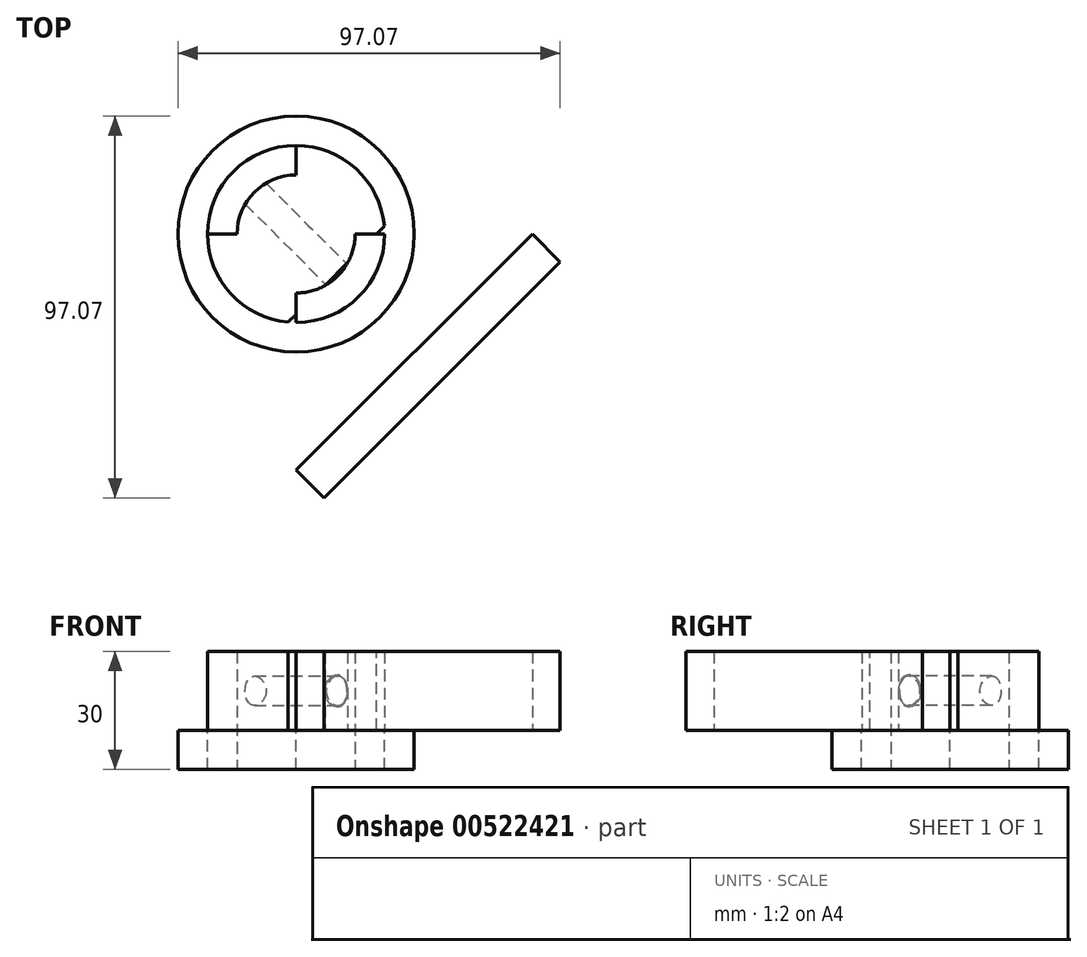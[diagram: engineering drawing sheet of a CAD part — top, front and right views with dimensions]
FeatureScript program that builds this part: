
annotation { "Feature Type Name" : "Feature", "Feature Type Description" : "" }
export const myFeature = defineFeature(function(context is Context, id is Id, definition is map)
    precondition{}
    {
        {
            var Q0;
            Q0=qCreatedBy(makeId("Top.planeOp"),FACE);
            var sketch = newSketch(context, id + "F0", { "sketchPlane" : qUnion([Q0])});
            skCircle(sketch, "E0", {"center": v(0, 0) * mm, "radius": 15 * mm});
            skCircle(sketch, "E1", {"center": v(0, 0) * mm, "radius": 30 * mm});
            skCircle(sketch, "E2", {"center": v(0, 0) * mm, "radius": 22.5 * mm});
            skLineSegment(sketch, "E3", {"start": v(0, 15) * mm, "end": v(0, 22.5) * mm});
            skLineSegment(sketch, "E4", {"start": v(0, 22.5) * mm, "end": v(0, 30) * mm, "construction": true});
            skLineSegment(sketch, "E5", {"start": v(-22.5, 0) * mm, "end": v(-15, 0) * mm});
            skLineSegment(sketch, "E6", {"start": v(0, -15) * mm, "end": v(0, -22.5) * mm});
            skLineSegment(sketch, "E7", {"start": v(15, 0) * mm, "end": v(22.5, 0) * mm});
            skSolve(sketch);
        }
        {
            var Q0;
            {var subQ0=sQuery(id+"F0.wireOp",EDGE,"E0");var subQ1=makeQuery(id+"F0.imprint","INTERSECT",VERTEX,{"derivedFrom":[subQ0,sQuery(id+"F0.wireOp",EDGE,"E3")]});Q0=makeQuery(id+"F0.imprint","IMPRINT",FACE,{"disambiguationData":[TD([[makeQuery(id+"F0.imprint","IMPRINT",EDGE,{"disambiguationData":[TD([[subQ1,1.0]])],"derivedFrom":subQ0}),1.0]])]});}
            var Q1;
            {var subQ0=sQuery(id+"F0.wireOp",EDGE,"E3");Q1=makeQuery(id+"F0.imprint","IMPRINT",FACE,{"disambiguationData":[TD([[makeQuery(id+"F0.imprint","IMPRINT",EDGE,{"derivedFrom":subQ0}),-1.0]])]});}
            var Q2;
            {var subQ0=sQuery(id+"F0.wireOp",EDGE,"E5");Q2=makeQuery(id+"F0.imprint","IMPRINT",FACE,{"disambiguationData":[TD([[makeQuery(id+"F0.imprint","IMPRINT",EDGE,{"derivedFrom":subQ0}),-1.0]])]});}
            extrude(context, id + "F1", {"entities" : qUnion([Q0, Q1, Q2]), "depth" : 20 * mm, "offsetDistance" : 25 * mm});
        }
        {
            var Q0;
            Q0=makeQuery(id+"F0.imprint","IMPRINT",FACE,{"disambiguationData":[TD([[makeQuery(id+"F0.imprint","IMPRINT",EDGE,{"derivedFrom":sQuery(id+"F0.wireOp",EDGE,"E1")}),1.0]])]});
            var Q1;
            {var subQ0=sQuery(id+"F0.wireOp",EDGE,"E3");Q1=makeQuery(id+"F0.imprint","IMPRINT",FACE,{"disambiguationData":[TD([[makeQuery(id+"F0.imprint","IMPRINT",EDGE,{"derivedFrom":subQ0}),-1.0]])]});}
            var Q2;
            {var subQ0=sQuery(id+"F0.wireOp",EDGE,"E0");var subQ1=makeQuery(id+"F0.imprint","INTERSECT",VERTEX,{"derivedFrom":[subQ0,sQuery(id+"F0.wireOp",EDGE,"E3")]});Q2=makeQuery(id+"F0.imprint","IMPRINT",FACE,{"disambiguationData":[TD([[makeQuery(id+"F0.imprint","IMPRINT",EDGE,{"disambiguationData":[TD([[subQ1,1.0]])],"derivedFrom":subQ0}),1.0]])]});}
            var Q3;
            {var subQ0=sQuery(id+"F0.wireOp",EDGE,"E5");Q3=makeQuery(id+"F0.imprint","IMPRINT",FACE,{"disambiguationData":[TD([[makeQuery(id+"F0.imprint","IMPRINT",EDGE,{"derivedFrom":subQ0}),-1.0]])]});}
            extrude(context, id + "F2", {"entities" : qUnion([Q0, Q1, Q2, Q3]), "operationType" : NewBodyOperationType.ADD, "oppositeDirection" : true, "depth" : 10 * mm, "offsetDistance" : 25 * mm});
        }
        {
            var Q0;
            Q0=qCreatedBy(makeId("Top.planeOp"),FACE);
            var sketch = newSketch(context, id + "F3", { "sketchPlane" : qUnion([Q0])});
            skLineSegment(sketch, "E8", {"start": v(0, 0) * mm, "end": v(0, -60) * mm, "construction": true});
            skLineSegment(sketch, "E9", {"start": v(60, 0) * mm, "end": v(0, -60) * mm});
            skLineSegment(sketch, "E10.MirrorCS", {"start": v(7.07, -67.07) * mm, "end": v(67.07, -7.07) * mm});
            skLineSegment(sketch, "E11.MirrorCS", {"start": v(67.07, -7.07) * mm, "end": v(60, 0) * mm});
            skLineSegment(sketch, "E12.MirrorCS", {"start": v(0, -60) * mm, "end": v(7.07, -67.07) * mm});
            skPoint(sketch, "E13.end.orphan", {"position": v(-60, 0) * mm});
            skPoint(sketch, "E13.start.orphan", {"position": v(-67.07, -7.07) * mm});
            skPoint(sketch, "E14.end.orphan", {"position": v(-7.07, -67.07) * mm});
            skPoint(sketch, "E14.start.orphan", {"position": v(0, -60) * mm});
            skLineSegment(sketch, "E15", {"start": v(0, 0) * mm, "end": v(60, 0) * mm, "construction": true});
            skSolve(sketch);
        }
        {
            var Q0;
            Q0=makeQuery(id+"F3.imprint","IMPRINT",FACE,{"disambiguationData":[TD([[makeQuery(id+"F3.imprint","IMPRINT",EDGE,{"derivedFrom":sQuery(id+"F3.wireOp",EDGE,"E9")}),1.0]])]});
            extrude(context, id + "F4", {"entities" : qUnion([Q0]), "depth" : 20 * mm, "offsetDistance" : 25 * mm});
        }
        {
            var Q0;
            Q0=makeQuery(id+"F4.opExtrude","SWEPT_FACE",FACE,{"disambiguationData":[OSD([sQuery(id+"F3.wireOp",EDGE,"E9")])]});
            var sketch = newSketch(context, id + "F5", { "sketchPlane" : qUnion([Q0])});
            skLineSegment(sketch, "E16", {"start": v(-42.43, 20) * mm, "end": v(-42.43, 0) * mm});
            skLineSegment(sketch, "E17", {"start": v(0, 20) * mm, "end": v(0, 0) * mm});
            skLineSegment(sketch, "E18", {"start": v(-42.43, 10) * mm, "end": v(-42.43, 10) * mm});
            skCircle(sketch, "E19", {"center": v(0, 10) * mm, "radius": 3.75 * mm});
            skCircle(sketch, "E20", {"center": v(0, 10) * mm, "radius": 4 * mm});
            skSolve(sketch);
        }
        {
            var Q0;
            {var subQ0=sQuery(id+"F5.wireOp",EDGE,"E19");var subQ1=sQuery(id+"F5.wireOp",EDGE,"E17");var subQ2=makeQuery(id+"F5.imprint","INTERSECT",VERTEX,{"disambiguationData":[OD(0.0)],"derivedFrom":[subQ1,subQ0]});Q0=makeQuery(id+"F5.imprint","IMPRINT",FACE,{"disambiguationData":[TD([[makeQuery(id+"F5.imprint","IMPRINT",EDGE,{"disambiguationData":[TD([[subQ2,-1.0]])],"derivedFrom":subQ1}),-1.0]])]});}
            var Q1;
            {var subQ0=sQuery(id+"F5.wireOp",EDGE,"E19");var subQ1=sQuery(id+"F5.wireOp",EDGE,"E17");var subQ2=makeQuery(id+"F5.imprint","INTERSECT",VERTEX,{"disambiguationData":[OD(0.0)],"derivedFrom":[subQ1,subQ0]});Q1=makeQuery(id+"F5.imprint","IMPRINT",FACE,{"disambiguationData":[TD([[makeQuery(id+"F5.imprint","IMPRINT",EDGE,{"disambiguationData":[TD([[subQ2,-1.0]])],"derivedFrom":subQ1}),1.0]])]});}
            var Q2;
            Q2=sQuery(id+"F5.wireOp",EDGE,"E19");
            extrude(context, id + "F6", {"entities" : qUnion([Q0, Q1]), "operationType" : NewBodyOperationType.REMOVE, "surfaceEntities" : qUnion([Q2]), "depth" : 60 * mm, "offsetDistance" : 25 * mm});
        }
        {
            var Q0;
            {var subQ0=sQuery(id+"F5.wireOp",EDGE,"E20");var subQ1=sQuery(id+"F5.wireOp",EDGE,"E17");var subQ2=makeQuery(id+"F5.imprint","INTERSECT",VERTEX,{"disambiguationData":[OD(0.0)],"derivedFrom":[subQ1,subQ0]});Q0=makeQuery(id+"F5.imprint","IMPRINT",FACE,{"disambiguationData":[TD([[makeQuery(id+"F5.imprint","IMPRINT",EDGE,{"disambiguationData":[TD([[subQ2,-1.0]])],"derivedFrom":subQ1}),-1.0]])]});}
            var Q1;
            {var subQ0=sQuery(id+"F5.wireOp",EDGE,"E20");var subQ1=sQuery(id+"F5.wireOp",EDGE,"E17");var subQ2=makeQuery(id+"F5.imprint","INTERSECT",VERTEX,{"disambiguationData":[OD(0.0)],"derivedFrom":[subQ1,subQ0]});Q1=makeQuery(id+"F5.imprint","IMPRINT",FACE,{"disambiguationData":[TD([[makeQuery(id+"F5.imprint","IMPRINT",EDGE,{"disambiguationData":[TD([[subQ2,-1.0]])],"derivedFrom":subQ1}),1.0]])]});}
            extrude(context, id + "F7", {"entities" : qUnion([Q0, Q1]), "operationType" : NewBodyOperationType.REMOVE, "depth" : 28 * mm, "offsetDistance" : 25 * mm});
        }
    });
